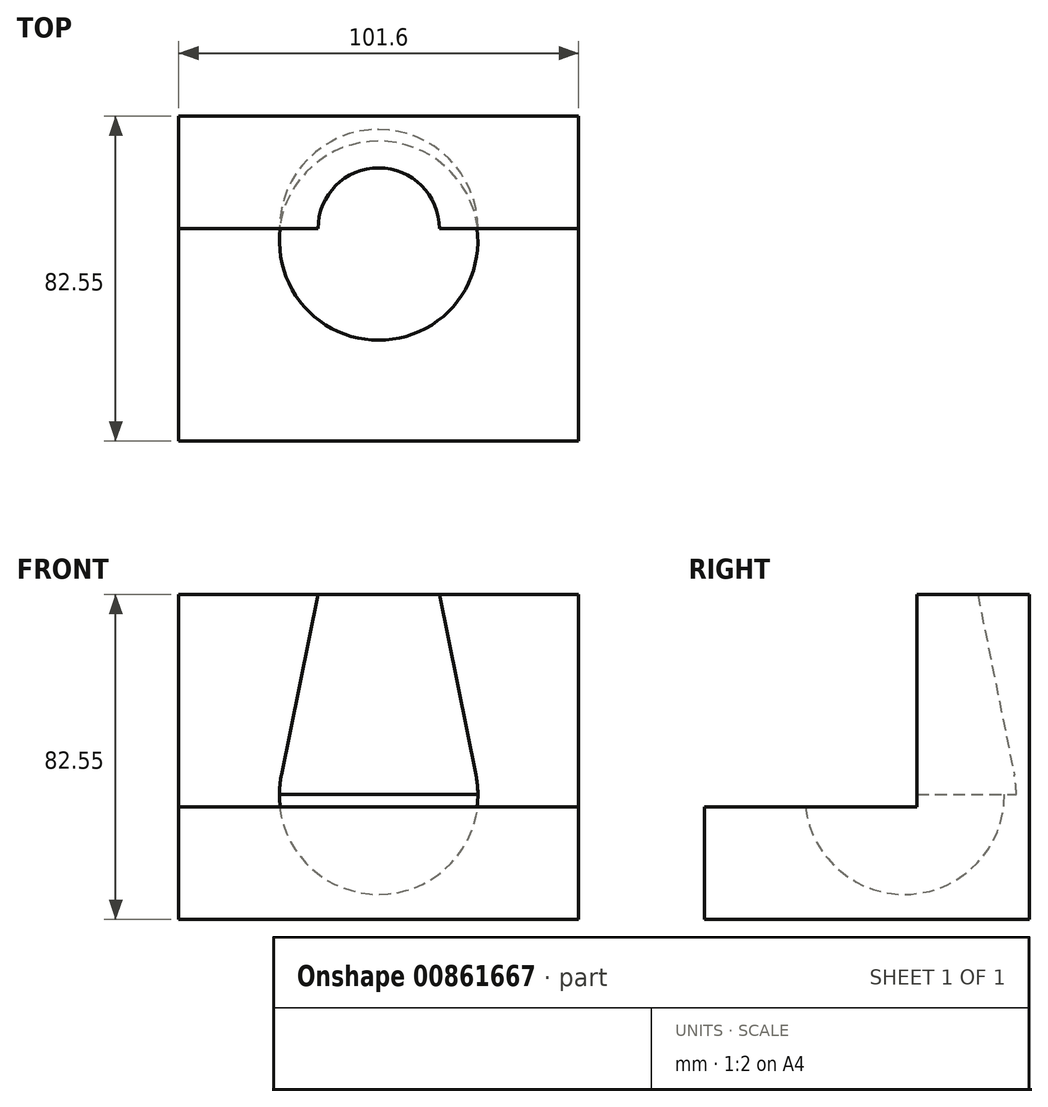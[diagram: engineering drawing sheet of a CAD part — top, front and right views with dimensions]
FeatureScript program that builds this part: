
annotation { "Feature Type Name" : "Feature", "Feature Type Description" : "" }
export const myFeature = defineFeature(function(context is Context, id is Id, definition is map)
    precondition{}
    {
        {
            var Q0;
            Q0=qCreatedBy(makeId("Right.planeOp"),FACE);
            var sketch = newSketch(context, id + "F0", { "sketchPlane" : qUnion([Q0])});
            skLineSegment(sketch, "E0", {"start": v(0, 0) * mm, "end": v(-50.8, 0) * mm});
            skLineSegment(sketch, "E1", {"start": v(-50.8, 0) * mm, "end": v(-50.8, -31.75) * mm});
            skLineSegment(sketch, "E2", {"start": v(-50.8, -31.75) * mm, "end": v(31.75, -31.75) * mm});
            skLineSegment(sketch, "E3", {"start": v(0, 0) * mm, "end": v(0, 50.8) * mm});
            skLineSegment(sketch, "E4", {"start": v(0, 50.8) * mm, "end": v(31.75, 50.8) * mm});
            skLineSegment(sketch, "E5", {"start": v(31.75, 50.8) * mm, "end": v(31.75, -31.75) * mm});
            skSolve(sketch);
        }
        {
            var Q0;
            Q0 = qSketchRegion(id + "F0", true);
            extrude(context, id + "F1", {"entities" : qUnion([Q0]), "depth" : 101.6 * mm, "offsetDistance" : 25.4 * mm});
        }
        {
            var Q0;
            Q0=makeQuery(id+"F1.opExtrude","SWEPT_FACE",FACE,{"disambiguationData":[OSD([sQuery(id+"F0.wireOp",EDGE,"E0")])]});
            var sketch = newSketch(context, id + "F2", { "sketchPlane" : qUnion([Q0])});
            skArc(sketch, "E6", {"start": v(25.4, 0) * mm, "mid": v(50.8, -25.4) * mm, "end": v(76.2, 0) * mm});
            skLineSegment(sketch, "E7", {"start": v(25.4, 0) * mm, "end": v(76.2, 0) * mm});
            skSolve(sketch);
        }
        {
            var Q0;
            Q0 = qSketchRegion(id + "F2", true);
            var Q1;
            Q1=sQuery(id+"F2.wireOp",EDGE,"E7");
            revolve(context, id + "F3", {"operationType" : NewBodyOperationType.REMOVE, "surfaceOperationType" : NewSurfaceOperationType.NEW, "entities" : qUnion([Q0]), "axis" : qUnion([Q1]), "revolveType" : RevolveType.FULL, "oppositeDirection" : true});
        }
        {
            var Q0;
            Q0=qCreatedBy(makeId("Right.planeOp"),FACE);
            var sketch = newSketch(context, id + "F4", { "sketchPlane" : qUnion([Q0])});
            skLineSegment(sketch, "E8.0", {"start": v(0, 0) * mm, "end": v(-50.8, 0) * mm});
            skLineSegment(sketch, "E9.0", {"start": v(0, 0) * mm, "end": v(0, 50.8) * mm});
            skLineSegment(sketch, "E10.0", {"start": v(3.18, -3.18) * mm, "end": v(-50.8, -3.18) * mm});
            skLineSegment(sketch, "E10.1", {"start": v(3.18, -3.17) * mm, "end": v(3.18, 50.8) * mm});
            skLineSegment(sketch, "E11", {"start": v(-50.8, -3.18) * mm, "end": v(-50.8, 0) * mm});
            skLineSegment(sketch, "E12", {"start": v(0, 50.8) * mm, "end": v(3.18, 50.8) * mm});
            skSolve(sketch);
        }
        {
            var Q0;
            Q0 = qSketchRegion(id + "F4", true);
            extrude(context, id + "F5", {"entities" : qUnion([Q0]), "operationType" : NewBodyOperationType.REMOVE, "depth" : 250.44 * mm, "offsetDistance" : 25.4 * mm});
        }
        {
            var Q0;
            Q0=makeQuery(id+"F5.boolean.opBoolean","COPY",FACE,{"derivedFrom":makeQuery(id+"F5.opExtrude","SWEPT_FACE",FACE,{"disambiguationData":[OSD([sQuery(id+"F4.wireOp",EDGE,"E10.1")])]})});
            var sketch = newSketch(context, id + "F6", { "sketchPlane" : qUnion([Q0])});
            skLineSegment(sketch, "E13", {"start": v(25.6, 0) * mm, "end": v(50.8, 0) * mm});
            skLineSegment(sketch, "E14", {"start": v(50.8, 0) * mm, "end": v(50.8, 50.8) * mm});
            skLineSegment(sketch, "E15", {"start": v(50.8, 50.8) * mm, "end": v(35.4, 50.8) * mm});
            skLineSegment(sketch, "E16", {"start": v(35.4, 50.8) * mm, "end": v(26.1, 5.01) * mm});
            skPoint(sketch, "E17.orphan", {"position": v(25.6, 0) * mm});
            skPoint(sketch, "E18.orphan", {"position": v(25.09, 0) * mm});
            skArc(sketch, "E19.trimOffspring", {"start": v(26.1, 5.01) * mm, "mid": v(25.73, 2.52) * mm, "end": v(25.6, 0) * mm});
            skPoint(sketch, "E20.0.start.orphan", {"position": v(75.8, -3.17) * mm});
            skPoint(sketch, "E21.orphan", {"position": v(25.8, -3.17) * mm});
            skSolve(sketch);
        }
        {
            var Q0;
            Q0 = qSketchRegion(id + "F6", true);
            var Q1;
            Q1=sQuery(id+"F6.wireOp",EDGE,"E14");
            revolve(context, id + "F7", {"operationType" : NewBodyOperationType.REMOVE, "surfaceOperationType" : NewSurfaceOperationType.NEW, "entities" : qUnion([Q0]), "axis" : qUnion([Q1]), "revolveType" : RevolveType.FULL, "oppositeDirection" : true});
        }
    });
